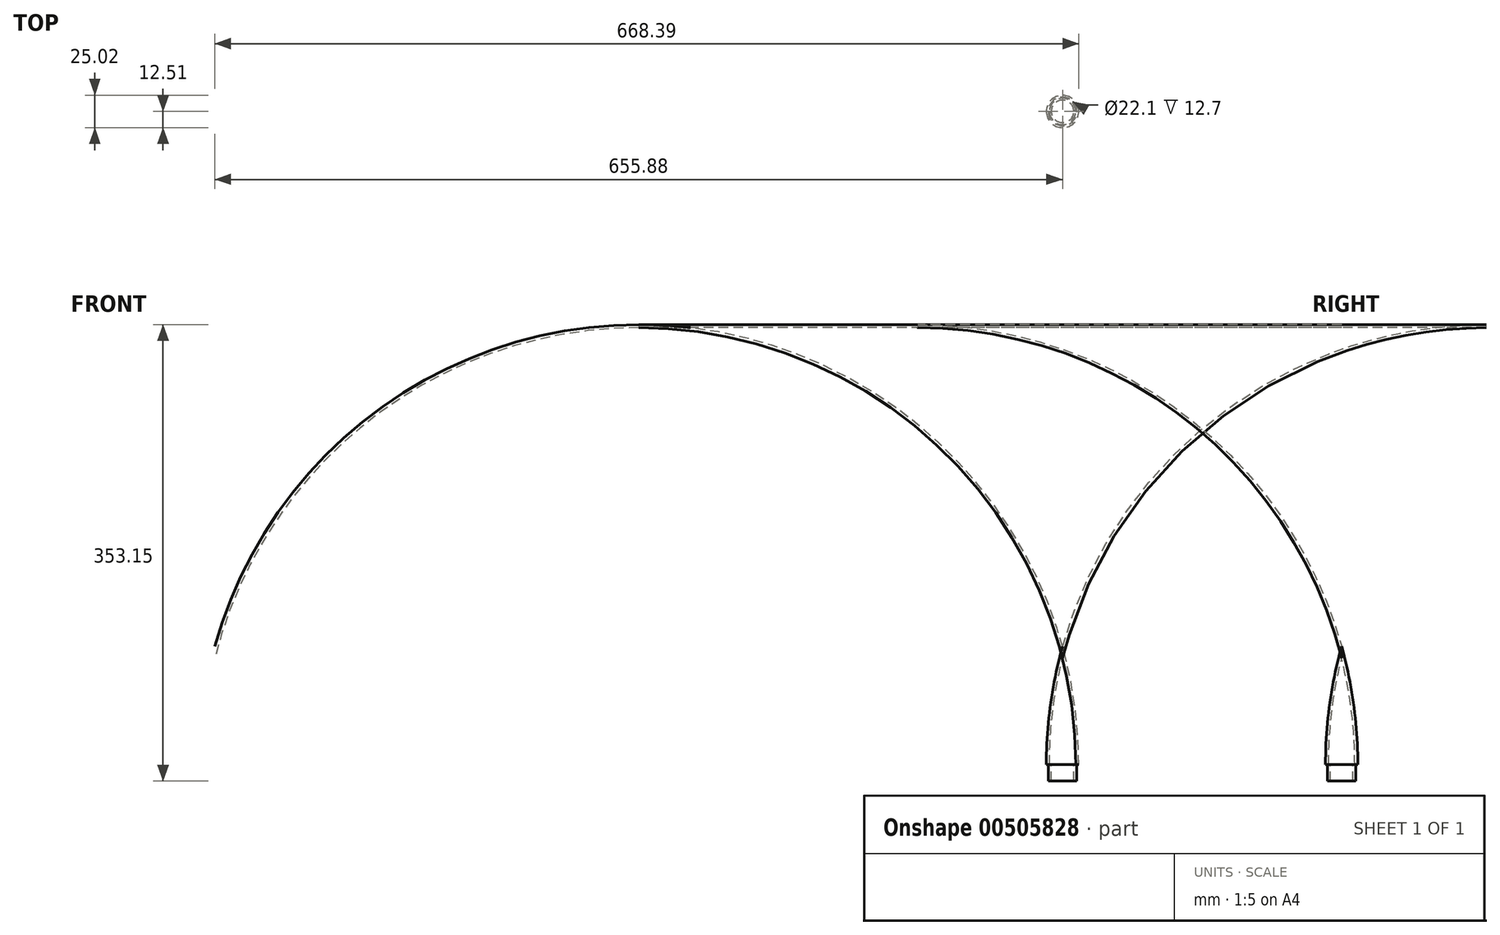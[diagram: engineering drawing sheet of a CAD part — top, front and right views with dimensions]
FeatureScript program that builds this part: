
annotation { "Feature Type Name" : "Feature", "Feature Type Description" : "" }
export const myFeature = defineFeature(function(context is Context, id is Id, definition is map)
    precondition{}
    {
        {
            var Q0;
            Q0=qCreatedBy(makeId("Front.planeOp"),FACE);
            var sketch = newSketch(context, id + "F0", { "sketchPlane" : qUnion([Q0])});
            skArc(sketch, "E0", {"start": v(0, 91.44) * mm, "mid": v(-9.37, 46.15) * mm, "end": v(-12.5, 0) * mm});
            skArc(sketch, "E1", {"start": v(0, 82.2) * mm, "mid": v(-7.6, 41.42) * mm, "end": v(-10.15, 0) * mm});
            skLineSegment(sketch, "E2", {"start": v(0, 82.2) * mm, "end": v(0, 91.44) * mm});
            skLineSegment(sketch, "E3", {"start": v(-12.5, 0) * mm, "end": v(-10.15, 0) * mm});
            skSolve(sketch);
        }
        {
            var Q0;
            Q0=qSketchRegion(id+"F0",true);
            var Q1;
            Q1=sQuery(id+"F0.wireOp",EDGE,"E2");
            revolve(context, id + "F1", {"entities" : qUnion([Q0]), "axis" : qUnion([Q1]), "revolveType" : RevolveType.FULL});
        }
        {
            var Q0;
            Q0=qCreatedBy(makeId("Top.planeOp"),FACE);
            var sketch = newSketch(context, id + "F2", { "sketchPlane" : qUnion([Q0])});
            skCircle(sketch, "E4", {"center": v(0, 0) * mm, "radius": 11.05 * mm});
            skCircle(sketch, "E5", {"center": v(0, 0) * mm, "radius": 8.69 * mm});
            skSolve(sketch);
        }
        {
            var Q0;
            Q0=makeQuery(id+"F2.imprint","IMPRINT",FACE,{"disambiguationData":[TD([[makeQuery(id+"F2.imprint","IMPRINT",EDGE,{"derivedFrom":sQuery(id+"F2.wireOp",EDGE,"E4")}),1.0]])]});
            extrude(context, id + "F3", {"entities" : qUnion([Q0]), "operationType" : NewBodyOperationType.ADD, "oppositeDirection" : true, "depth" : 12.7 * mm});
        }
    });
